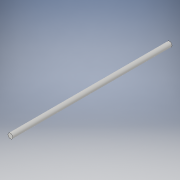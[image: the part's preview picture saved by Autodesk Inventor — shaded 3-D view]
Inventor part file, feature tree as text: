
AUTODESK INVENTOR PART (.ipt)
format: ipt  version: 2019 (Build 230136000, 136)  size: 95,744 bytes
history: native  units: mm
features: other x1, extrude x1, sketch x1
ambient origin geometry x8: Origin, YZ Plane, XZ Plane, XY Plane, X Axis, Y Axis, Z Axis, Center Point
bodies: Body1 (feature_tree)
feature tree (3):
  other  "ソリッド1"
  extrude  "押し出し1"  Depth=2.0mm
  sketch  "スケッチ1"
